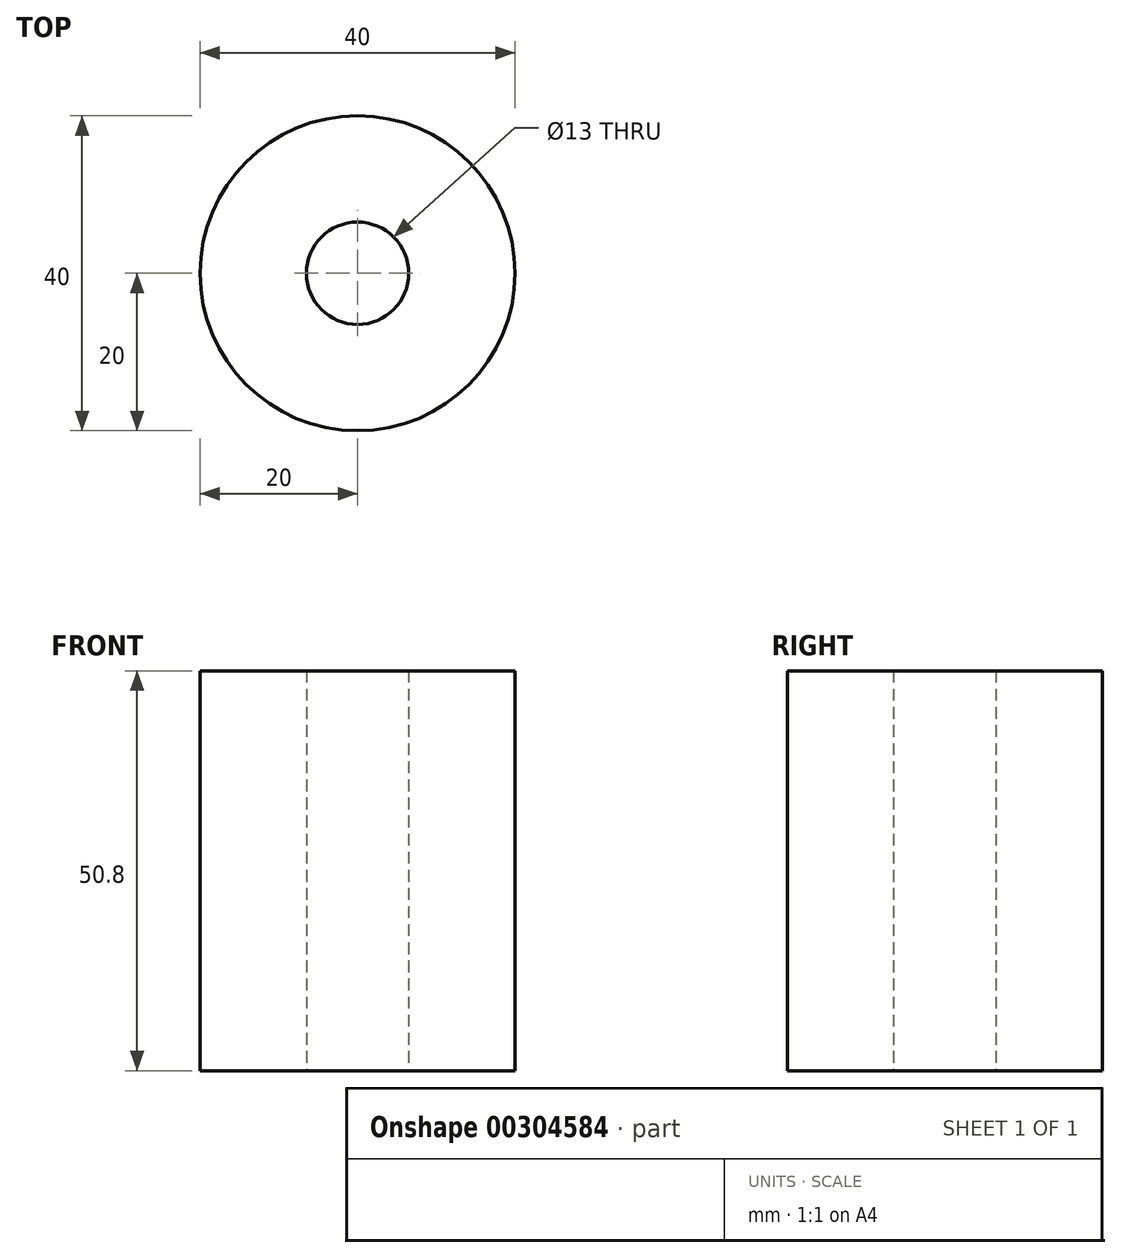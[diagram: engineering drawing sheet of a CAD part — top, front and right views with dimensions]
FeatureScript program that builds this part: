
annotation { "Feature Type Name" : "Feature", "Feature Type Description" : "" }
export const myFeature = defineFeature(function(context is Context, id is Id, definition is map)
    precondition{}
    {
        {
            var Q0;
            Q0=qCreatedBy(makeId("Top.planeOp"),FACE);
            var sketch = newSketch(context, id + "F0", { "sketchPlane" : qUnion([Q0])});
            skCircle(sketch, "E0", {"center": v(0, 0) * mm, "radius": 20 * mm});
            skCircle(sketch, "E1", {"center": v(0, 0) * mm, "radius": 6.5 * mm});
            skSolve(sketch);
        }
        {
            var Q0;
            Q0=makeQuery(id+"F0.imprint","IMPRINT",FACE,{"disambiguationData":[TD([[makeQuery(id+"F0.imprint","IMPRINT",EDGE,{"derivedFrom":sQuery(id+"F0.wireOp",EDGE,"E0")}),1.0]])]});
            extrude(context, id + "F1", {"entities" : qUnion([Q0]), "depth" : 50.8 * mm});
        }
    });
